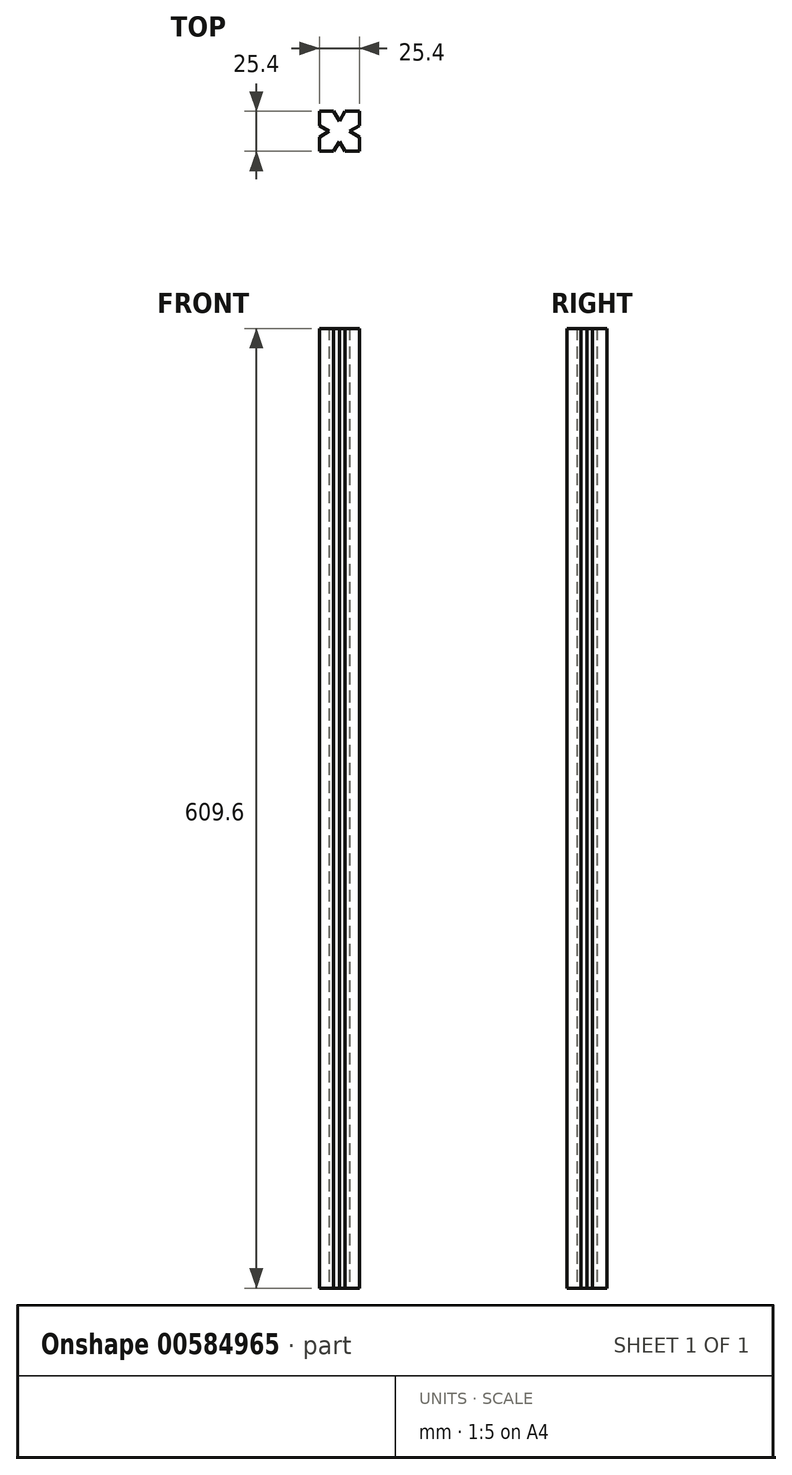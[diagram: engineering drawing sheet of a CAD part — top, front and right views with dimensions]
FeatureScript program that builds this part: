
annotation { "Feature Type Name" : "Feature", "Feature Type Description" : "" }
export const myFeature = defineFeature(function(context is Context, id is Id, definition is map)
    precondition{}
    {
        {
            var Q0;
            Q0=qCreatedBy(makeId("Top.planeOp"),FACE);
            var sketch = newSketch(context, id + "F0", { "sketchPlane" : qUnion([Q0])});
            skLineSegment(sketch, "E0.bottom", {"start": v(12.7, -12.7) * mm, "end": v(3.64, -12.7) * mm});
            skLineSegment(sketch, "E0.top", {"start": v(12.7, 12.7) * mm, "end": v(3.64, 12.7) * mm});
            skLineSegment(sketch, "E0.left", {"start": v(12.7, -12.7) * mm, "end": v(12.7, -3.64) * mm});
            skLineSegment(sketch, "E0.right", {"start": v(-12.7, -12.7) * mm, "end": v(-12.7, -3.64) * mm});
            skPoint(sketch, "E0.middle", {"position": v(0, 0) * mm});
            skLineSegment(sketch, "E1.1", {"start": v(12.7, -3.64) * mm, "end": v(6.39, 0) * mm});
            skLineSegment(sketch, "E1.2", {"start": v(6.39, 0) * mm, "end": v(12.7, 3.64) * mm});
            skPoint(sketch, "E1.0.midPoint", {"position": v(15.86, 0) * mm});
            skLineSegment(sketch, "E2.1.0", {"start": v(3.64, 12.7) * mm, "end": v(0, 6.39) * mm});
            skLineSegment(sketch, "E2.1.2", {"start": v(0, 6.39) * mm, "end": v(-3.64, 12.7) * mm});
            skLineSegment(sketch, "E2.2.0", {"start": v(-12.7, 3.64) * mm, "end": v(-6.39, 0) * mm});
            skLineSegment(sketch, "E2.2.2", {"start": v(-6.39, 0) * mm, "end": v(-12.7, -3.64) * mm});
            skLineSegment(sketch, "E2.3.0", {"start": v(-3.64, -12.7) * mm, "end": v(0, -6.39) * mm});
            skLineSegment(sketch, "E2.3.2", {"start": v(0, -6.39) * mm, "end": v(3.64, -12.7) * mm});
            skPoint(sketch, "E3.orphan", {"position": v(-5.47, 15.86) * mm});
            skPoint(sketch, "E4.orphan", {"position": v(5.47, 15.86) * mm});
            skPoint(sketch, "E5.orphan", {"position": v(15.86, 5.47) * mm});
            skPoint(sketch, "E6.orphan", {"position": v(15.86, -5.47) * mm});
            skPoint(sketch, "E7.orphan", {"position": v(-15.86, 5.47) * mm});
            skPoint(sketch, "E1.cCircle.center.orphan", {"position": v(12.7, 0) * mm});
            skLineSegment(sketch, "E8.trimOffspring", {"start": v(12.7, 3.64) * mm, "end": v(12.7, 12.7) * mm});
            skLineSegment(sketch, "E9.trimOffspring", {"start": v(-3.64, -12.7) * mm, "end": v(-12.7, -12.7) * mm});
            skLineSegment(sketch, "E10.trimOffspring", {"start": v(-12.7, 3.64) * mm, "end": v(-12.7, 12.7) * mm});
            skLineSegment(sketch, "E11.trimOffspring", {"start": v(-3.64, 12.7) * mm, "end": v(-12.7, 12.7) * mm});
            skSolve(sketch);
        }
        {
            var Q0;
            Q0=makeQuery(id+"F0.imprint","IMPRINT",FACE,{"disambiguationData":[TD([[makeQuery(id+"F0.imprint","IMPRINT",EDGE,{"derivedFrom":sQuery(id+"F0.wireOp",EDGE,"E0.bottom")}),-1.0]])]});
            extrude(context, id + "F1", {"entities" : qUnion([Q0]), "depth" : 609.6 * mm, "offsetDistance" : 25.4 * mm});
        }
    });
